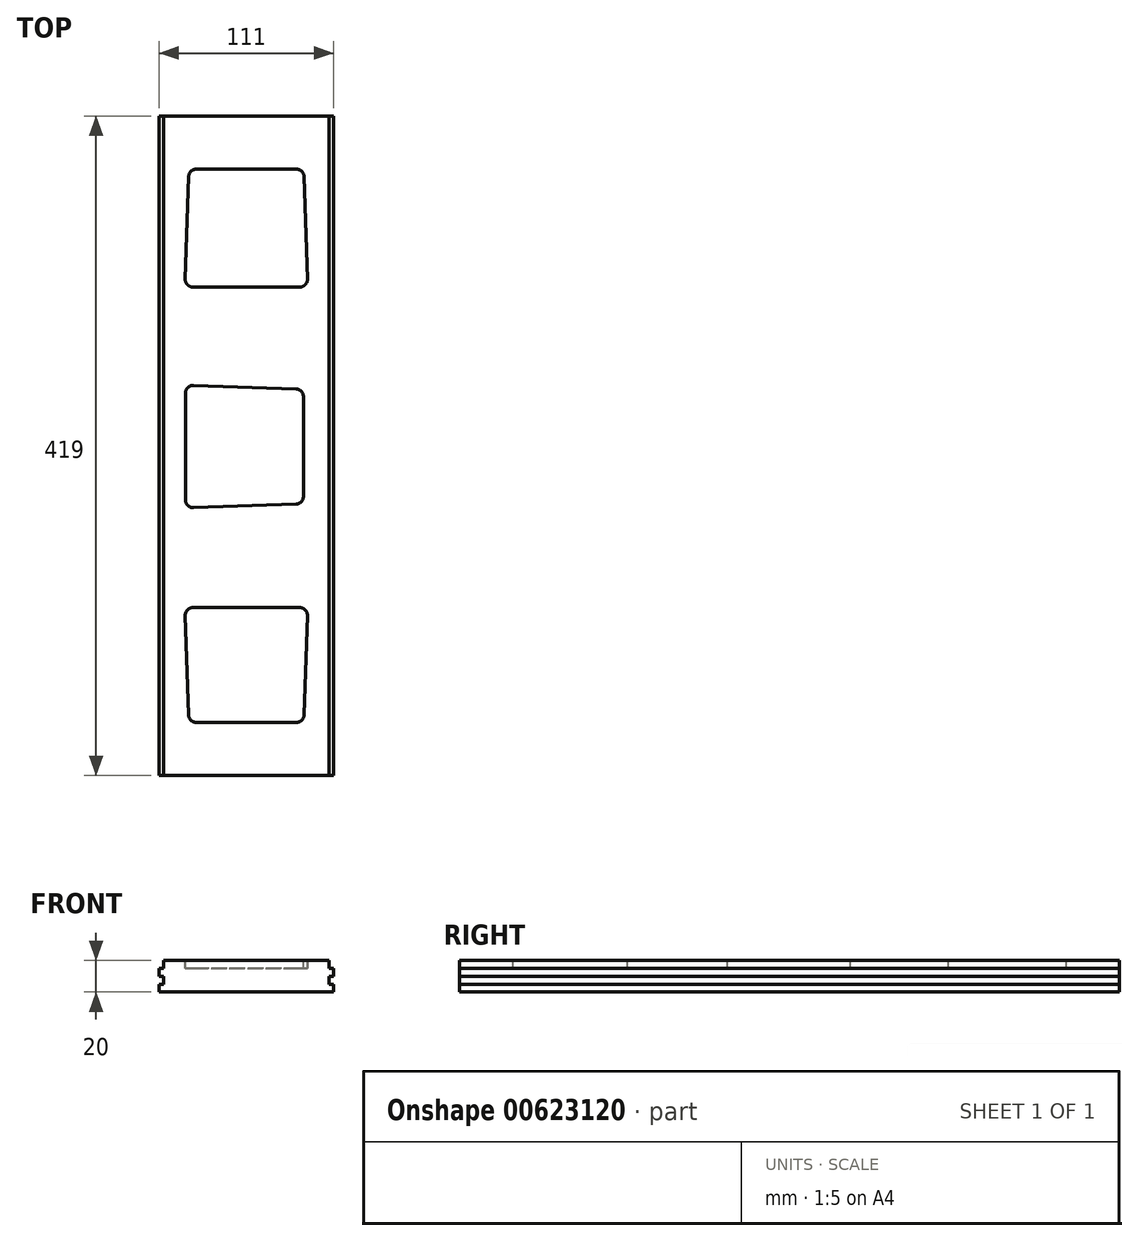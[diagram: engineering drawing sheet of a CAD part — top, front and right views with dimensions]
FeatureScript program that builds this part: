
annotation { "Feature Type Name" : "Feature", "Feature Type Description" : "" }
export const myFeature = defineFeature(function(context is Context, id is Id, definition is map)
    precondition{}
    {
        {
            var Q0;
            Q0=qCreatedBy(makeId("Front.planeOp"),FACE);
            var sketch = newSketch(context, id + "F0", { "sketchPlane" : qUnion([Q0])});
            skLineSegment(sketch, "E0", {"start": v(0, 0) * mm, "end": v(55.5, 0) * mm});
            skLineSegment(sketch, "E1", {"start": v(55.5, 0) * mm, "end": v(55.5, 4.9) * mm});
            skLineSegment(sketch, "E2", {"start": v(55.5, 4.9) * mm, "end": v(52.4, 4.9) * mm});
            skLineSegment(sketch, "E3", {"start": v(52.4, 4.9) * mm, "end": v(52.4, 10.1) * mm});
            skLineSegment(sketch, "E4", {"start": v(52.4, 10.1) * mm, "end": v(55.5, 10.1) * mm});
            skLineSegment(sketch, "E5", {"start": v(55.5, 10.1) * mm, "end": v(55.5, 15) * mm});
            skLineSegment(sketch, "E6", {"start": v(55.5, 15) * mm, "end": v(52.4, 15) * mm});
            skLineSegment(sketch, "E7", {"start": v(52.4, 15) * mm, "end": v(52.4, 20) * mm});
            skLineSegment(sketch, "E8", {"start": v(52.4, 20) * mm, "end": v(0, 20) * mm});
            skLineSegment(sketch, "E9", {"start": v(67.5, 20) * mm, "end": v(67.5, 0) * mm, "construction": true});
            skLineSegment(sketch, "E10", {"start": v(0, 33.55) * mm, "end": v(0, -32.51) * mm, "construction": true});
            skLineSegment(sketch, "E11.MirrorCS", {"start": v(-55.5, 0) * mm, "end": v(-55.5, 4.9) * mm});
            skLineSegment(sketch, "E12.MirrorCS", {"start": v(-55.5, 15) * mm, "end": v(-52.4, 15) * mm});
            skLineSegment(sketch, "E13.MirrorCS", {"start": v(-55.5, 4.9) * mm, "end": v(-52.4, 4.9) * mm});
            skLineSegment(sketch, "E14.MirrorCS", {"start": v(-55.5, 10.1) * mm, "end": v(-55.5, 15) * mm});
            skLineSegment(sketch, "E15.MirrorCS", {"start": v(-52.4, 15) * mm, "end": v(-52.4, 20) * mm});
            skLineSegment(sketch, "E16.MirrorCS", {"start": v(-52.4, 4.9) * mm, "end": v(-52.4, 10.1) * mm});
            skLineSegment(sketch, "E17.MirrorCS", {"start": v(-52.4, 10.1) * mm, "end": v(-55.5, 10.1) * mm});
            skLineSegment(sketch, "E18.MirrorCS", {"start": v(-52.4, 20) * mm, "end": v(0, 20) * mm});
            skLineSegment(sketch, "E19.MirrorCS", {"start": v(0, 0) * mm, "end": v(-55.5, 0) * mm});
            skSolve(sketch);
        }
        {
            var Q0;
            Q0 = qSketchRegion(id + "F0", true);
            extrude(context, id + "F1", {"entities" : qUnion([Q0]), "oppositeDirection" : true, "depth" : 419 * mm, "offsetDistance" : 25 * mm});
        }
        {
            var Q0;
            Q0=makeQuery(id+"F1.opExtrude","SWEPT_FACE",FACE,{"disambiguationData":[OSD([sQuery(id+"F0.wireOp",EDGE,"E8"),sQuery(id+"F0.wireOp",EDGE,"E18.MirrorCS")])]});
            var sketch = newSketch(context, id + "F2", { "sketchPlane" : qUnion([Q0])});
            skLineSegment(sketch, "E20.bottom", {"start": v(-36.5, 385.26) * mm, "end": v(36.5, 385.26) * mm});
            skLineSegment(sketch, "E20.top", {"start": v(-39, 310.26) * mm, "end": v(39, 310.26) * mm});
            skLineSegment(sketch, "E21", {"start": v(0, 425.65) * mm, "end": v(0, -24.28) * mm, "construction": true});
            skLineSegment(sketch, "E22", {"start": v(36.5, 385.26) * mm, "end": v(39, 310.26) * mm});
            skLineSegment(sketch, "E23", {"start": v(-36.5, 385.26) * mm, "end": v(-39, 310.26) * mm});
            skLineSegment(sketch, "E24", {"start": v(-36.5, 385.26) * mm, "end": v(39, 310.26) * mm, "construction": true});
            skLineSegment(sketch, "E25", {"start": v(36.5, 385.26) * mm, "end": v(-39, 310.26) * mm, "construction": true});
            skLineSegment(sketch, "E26", {"start": v(-82.9, 279) * mm, "end": v(105.35, 279) * mm, "construction": true});
            skLineSegment(sketch, "E27", {"start": v(-82.9, 139) * mm, "end": v(107.2, 139) * mm, "construction": true});
            skPoint(sketch, "E28", {"position": v(0, 349) * mm});
            skLineSegment(sketch, "E29.1.0", {"start": v(36.5, 33.7) * mm, "end": v(-36.5, 33.7) * mm});
            skLineSegment(sketch, "E29.1.1", {"start": v(39, 106.7) * mm, "end": v(-39, 106.7) * mm});
            skPoint(sketch, "E29.1.2", {"position": v(0, 69) * mm});
            skLineSegment(sketch, "E29.1.3", {"start": v(-36.5, 33.7) * mm, "end": v(39, 106.7) * mm, "construction": true});
            skLineSegment(sketch, "E29.1.4", {"start": v(36.5, 33.7) * mm, "end": v(-39, 106.7) * mm, "construction": true});
            skLineSegment(sketch, "E29.1.5", {"start": v(36.5, 33.7) * mm, "end": v(39, 106.7) * mm});
            skLineSegment(sketch, "E29.1.6", {"start": v(-36.5, 33.7) * mm, "end": v(-39, 106.7) * mm});
            skLineSegment(sketch, "E29.1.8", {"start": v(36.5, 33.7) * mm, "end": v(-36.5, 33.7) * mm});
            skPoint(sketch, "E29.center", {"position": v(-94.71, 39.43) * mm});
            skPoint(sketch, "E30.1.0", {"position": v(0, 209) * mm});
            skLineSegment(sketch, "E30.1.1", {"start": v(36.26, 245.5) * mm, "end": v(-38.74, 248) * mm});
            skLineSegment(sketch, "E30.1.2", {"start": v(-38.74, 248) * mm, "end": v(-38.74, 170) * mm});
            skLineSegment(sketch, "E30.1.3", {"start": v(36.26, 245.5) * mm, "end": v(36.26, 172.5) * mm});
            skLineSegment(sketch, "E30.1.5", {"start": v(36.26, 172.5) * mm, "end": v(-38.74, 170) * mm});
            skLineSegment(sketch, "E30.1.6", {"start": v(36.26, 245.5) * mm, "end": v(-38.74, 170) * mm, "construction": true});
            skLineSegment(sketch, "E30.1.7", {"start": v(36.26, 172.5) * mm, "end": v(-38.74, 248) * mm, "construction": true});
            skLineSegment(sketch, "E30.1.8", {"start": v(36.26, 245.5) * mm, "end": v(36.26, 172.5) * mm});
            skSolve(sketch);
        }
        {
            var Q0;
            Q0 = qSketchRegion(id + "F2", true);
            extrude(context, id + "F3", {"entities" : qUnion([Q0]), "operationType" : NewBodyOperationType.REMOVE, "oppositeDirection" : true, "depth" : 5 * mm, "offsetDistance" : 25 * mm});
        }
        {
            var Q0;
            Q0=makeQuery(id+"F3.boolean.opBoolean","COPY",EDGE,{"derivedFrom":makeQuery(id+"F3.opExtrude","SWEPT_EDGE",EDGE,{"disambiguationData":[OSD([sQuery(id+"F2.wireOp",EDGE,"E20.bottom"),sQuery(id+"F2.wireOp",EDGE,"E23")])]})});
            var Q1;
            Q1=makeQuery(id+"F3.boolean.opBoolean","COPY",EDGE,{"derivedFrom":makeQuery(id+"F3.opExtrude","SWEPT_EDGE",EDGE,{"disambiguationData":[OSD([sQuery(id+"F2.wireOp",EDGE,"E20.bottom"),sQuery(id+"F2.wireOp",EDGE,"E22")])]})});
            var Q2;
            Q2=makeQuery(id+"F3.boolean.opBoolean","COPY",EDGE,{"derivedFrom":makeQuery(id+"F3.opExtrude","SWEPT_EDGE",EDGE,{"disambiguationData":[OSD([sQuery(id+"F2.wireOp",EDGE,"E20.top"),sQuery(id+"F2.wireOp",EDGE,"E23")])]})});
            var Q3;
            Q3=makeQuery(id+"F3.boolean.opBoolean","COPY",EDGE,{"derivedFrom":makeQuery(id+"F3.opExtrude","SWEPT_EDGE",EDGE,{"disambiguationData":[OSD([sQuery(id+"F2.wireOp",EDGE,"E20.top"),sQuery(id+"F2.wireOp",EDGE,"E22")])]})});
            var Q4;
            Q4=makeQuery(id+"F3.boolean.opBoolean","COPY",EDGE,{"derivedFrom":makeQuery(id+"F3.opExtrude","SWEPT_EDGE",EDGE,{"disambiguationData":[OSD([sQuery(id+"F2.wireOp",EDGE,"E30.1.1"),sQuery(id+"F2.wireOp",EDGE,"E30.1.2")])]})});
            var Q5;
            Q5=makeQuery(id+"F3.boolean.opBoolean","COPY",EDGE,{"derivedFrom":makeQuery(id+"F3.opExtrude","SWEPT_EDGE",EDGE,{"disambiguationData":[OSD([sQuery(id+"F2.wireOp",EDGE,"E30.1.1"),sQuery(id+"F2.wireOp",EDGE,"E30.1.8")])]})});
            var Q6;
            Q6=makeQuery(id+"F3.boolean.opBoolean","COPY",EDGE,{"derivedFrom":makeQuery(id+"F3.opExtrude","SWEPT_EDGE",EDGE,{"disambiguationData":[OSD([sQuery(id+"F2.wireOp",EDGE,"E29.1.1"),sQuery(id+"F2.wireOp",EDGE,"E29.1.5")])]})});
            var Q7;
            Q7=makeQuery(id+"F3.boolean.opBoolean","COPY",EDGE,{"derivedFrom":makeQuery(id+"F3.opExtrude","SWEPT_EDGE",EDGE,{"disambiguationData":[OSD([sQuery(id+"F2.wireOp",EDGE,"E29.1.1"),sQuery(id+"F2.wireOp",EDGE,"E29.1.6")])]})});
            var Q8;
            Q8=makeQuery(id+"F3.boolean.opBoolean","COPY",EDGE,{"derivedFrom":makeQuery(id+"F3.opExtrude","SWEPT_EDGE",EDGE,{"disambiguationData":[OSD([sQuery(id+"F2.wireOp",EDGE,"E30.1.2"),sQuery(id+"F2.wireOp",EDGE,"E30.1.5")])]})});
            var Q9;
            Q9=makeQuery(id+"F3.boolean.opBoolean","COPY",EDGE,{"derivedFrom":makeQuery(id+"F3.opExtrude","SWEPT_EDGE",EDGE,{"disambiguationData":[OSD([sQuery(id+"F2.wireOp",EDGE,"E30.1.5"),sQuery(id+"F2.wireOp",EDGE,"E30.1.8")])]})});
            var Q10;
            Q10=makeQuery(id+"F3.boolean.opBoolean","COPY",EDGE,{"derivedFrom":makeQuery(id+"F3.opExtrude","SWEPT_EDGE",EDGE,{"disambiguationData":[OSD([sQuery(id+"F2.wireOp",EDGE,"E29.1.5"),sQuery(id+"F2.wireOp",EDGE,"E29.1.8")])]})});
            var Q11;
            Q11=makeQuery(id+"F3.boolean.opBoolean","COPY",EDGE,{"derivedFrom":makeQuery(id+"F3.opExtrude","SWEPT_EDGE",EDGE,{"disambiguationData":[OSD([sQuery(id+"F2.wireOp",EDGE,"E29.1.6"),sQuery(id+"F2.wireOp",EDGE,"E29.1.8")])]})});
            fillet(context, id + "F4", {"entities" : qUnion([Q0, Q1, Q2, Q3, Q4, Q5, Q6, Q7, Q8, Q9, Q10, Q11]), "radius" : 5 * mm, "tangentPropagation" : true, "allowEdgeOverflow" : false});
        }
    });
